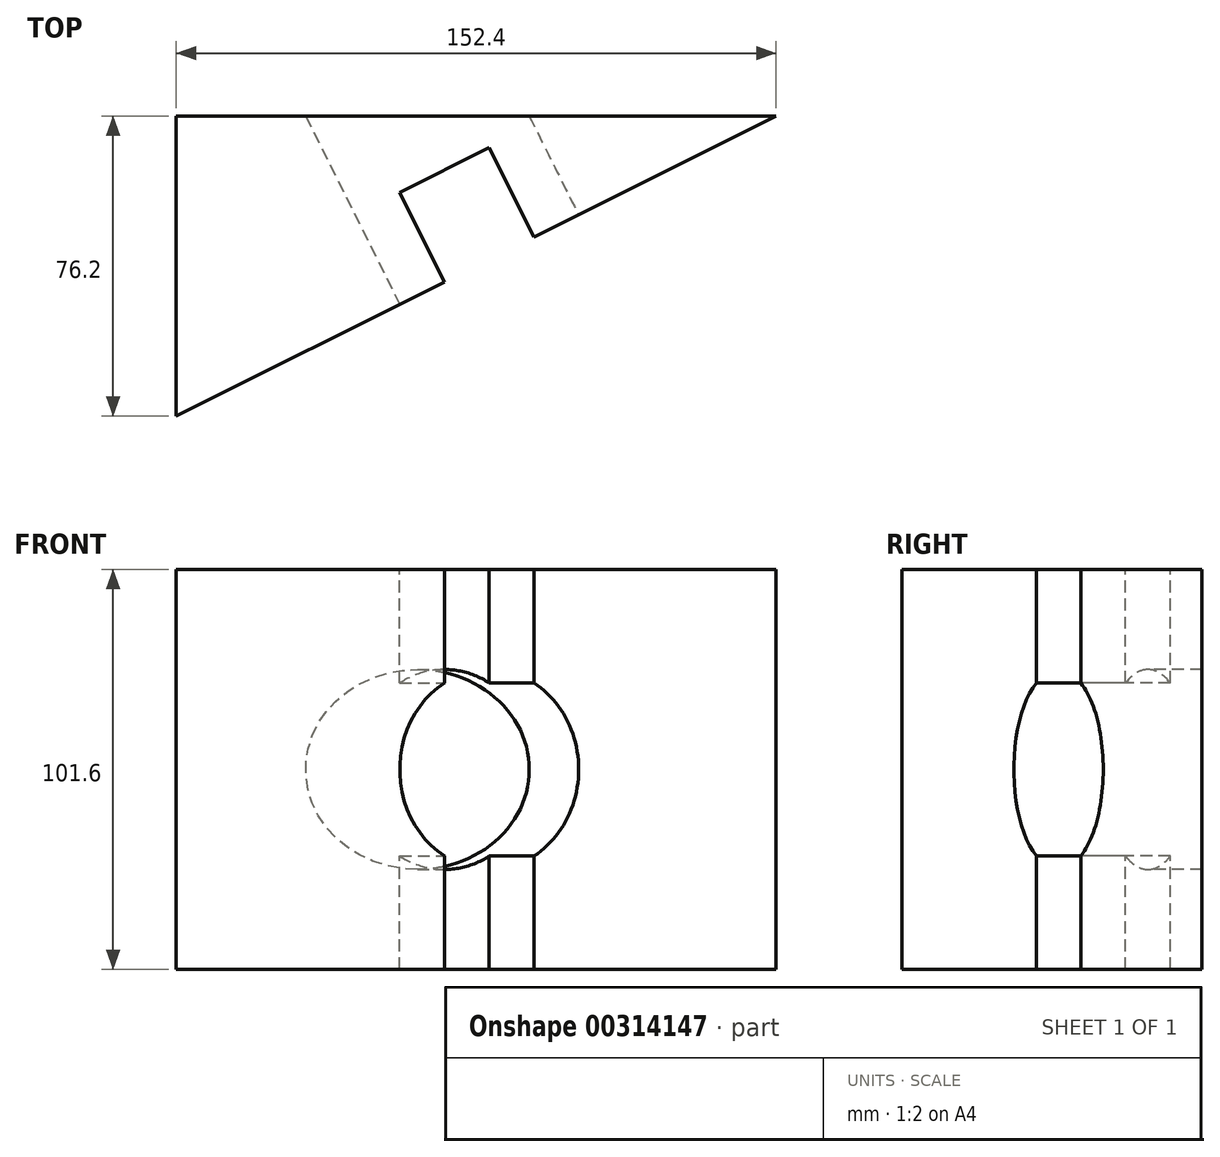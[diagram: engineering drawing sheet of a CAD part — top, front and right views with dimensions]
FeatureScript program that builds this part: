
annotation { "Feature Type Name" : "Feature", "Feature Type Description" : "" }
export const myFeature = defineFeature(function(context is Context, id is Id, definition is map)
    precondition{}
    {
        {
            var Q0;
            Q0=qCreatedBy(makeId("Top.planeOp"),FACE);
            var sketch = newSketch(context, id + "F0", { "sketchPlane" : qUnion([Q0])});
            skLineSegment(sketch, "E0.bottom", {"start": v(0, 0) * mm, "end": v(152.4, 0) * mm});
            skLineSegment(sketch, "E0.top", {"start": v(0, -76.2) * mm, "end": v(152.4, -76.2) * mm});
            skLineSegment(sketch, "E0.left", {"start": v(0, 0) * mm, "end": v(0, -76.2) * mm});
            skLineSegment(sketch, "E0.right", {"start": v(152.4, 0) * mm, "end": v(152.4, -76.2) * mm});
            skLineSegment(sketch, "E1", {"start": v(0, -76.2) * mm, "end": v(152.4, 0) * mm});
            skSolve(sketch);
        }
        {
            var Q0;
            Q0=makeQuery(id+"F0.imprint","IMPRINT",FACE,{"disambiguationData":[TD([[makeQuery(id+"F0.imprint","IMPRINT",EDGE,{"derivedFrom":sQuery(id+"F0.wireOp",EDGE,"E0.bottom")}),-1.0]])]});
            extrude(context, id + "F1", {"entities" : qUnion([Q0]), "depth" : 101.6 * mm});
        }
        {
            var Q0;
            Q0=makeQuery(id+"F1.opExtrude","SWEPT_FACE",FACE,{"disambiguationData":[OSD([sQuery(id+"F0.wireOp",EDGE,"E1")])]});
            var sketch = newSketch(context, id + "F2", { "sketchPlane" : qUnion([Q0])});
            skLineSegment(sketch, "E2.bottom", {"start": v(67.52, 0) * mm, "end": v(42.12, 0) * mm});
            skLineSegment(sketch, "E2.top", {"start": v(67.52, 101.6) * mm, "end": v(42.12, 101.6) * mm});
            skLineSegment(sketch, "E2.left", {"start": v(67.52, 0) * mm, "end": v(67.52, 101.6) * mm});
            skLineSegment(sketch, "E2.right", {"start": v(42.12, 0) * mm, "end": v(42.12, 101.6) * mm});
            skPoint(sketch, "E2.middle", {"position": v(54.82, 50.8) * mm});
            skSolve(sketch);
        }
        {
            var Q0;
            Q0=makeQuery(id+"F2.imprint","IMPRINT",FACE,{"disambiguationData":[TD([[makeQuery(id+"F2.imprint","IMPRINT",EDGE,{"derivedFrom":sQuery(id+"F2.wireOp",EDGE,"E2.bottom")}),1.0]])]});
            extrude(context, id + "F3", {"entities" : qUnion([Q0]), "operationType" : NewBodyOperationType.REMOVE, "oppositeDirection" : true, "depth" : 25.4 * mm});
        }
        {
            var Q0;
            {var subQ0=sQuery(id+"F2.wireOp",EDGE,"E2.right");Q0=makeQuery(id+"F2.imprint","IMPRINT",FACE,{"disambiguationData":[TD([[makeQuery(id+"F2.imprint","IMPRINT",EDGE,{"derivedFrom":subQ0}),1.0]])]});}
            var sketch = newSketch(context, id + "F4", { "sketchPlane" : qUnion([Q0])});
            skCircle(sketch, "E3", {"center": v(54.82, 50.8) * mm, "radius": 25.4 * mm});
            skSolve(sketch);
        }
        {
            var Q0;
            {var subQ0=sQuery(id+"F4.wireOp",EDGE,"E3");var subQ1=makeQuery(id+"F2.imprint","IMPRINT",EDGE,{"derivedFrom":sQuery(id+"F2.wireOp",EDGE,"E2.right")});var subQ2=makeQuery(id+"F4.imprint","INTERSECT",VERTEX,{"disambiguationData":[OD(0.0)],"derivedFrom":[subQ1,subQ0]});Q0=makeQuery(id+"F4.imprint","IMPRINT",FACE,{"disambiguationData":[TD([[makeQuery(id+"F4.imprint","IMPRINT",EDGE,{"disambiguationData":[TD([[subQ2,1.0]])],"derivedFrom":subQ0}),1.0]])]});}
            var Q1;
            {var subQ0=sQuery(id+"F4.wireOp",EDGE,"E3");var subQ1=makeQuery(id+"F2.imprint","IMPRINT",EDGE,{"derivedFrom":sQuery(id+"F2.wireOp",EDGE,"E2.right")});var subQ2=makeQuery(id+"F4.imprint","INTERSECT",VERTEX,{"disambiguationData":[OD(0.0)],"derivedFrom":[subQ1,subQ0]});Q1=makeQuery(id+"F4.imprint","IMPRINT",FACE,{"disambiguationData":[TD([[makeQuery(id+"F4.imprint","IMPRINT",EDGE,{"disambiguationData":[TD([[subQ2,-1.0]])],"derivedFrom":subQ0}),1.0]])]});}
            extrude(context, id + "F5", {"entities" : qUnion([Q0, Q1]), "operationType" : NewBodyOperationType.REMOVE, "endBound" : BoundingType.THROUGH_ALL, "oppositeDirection" : true, "depth" : 25.4 * mm});
        }
    });
